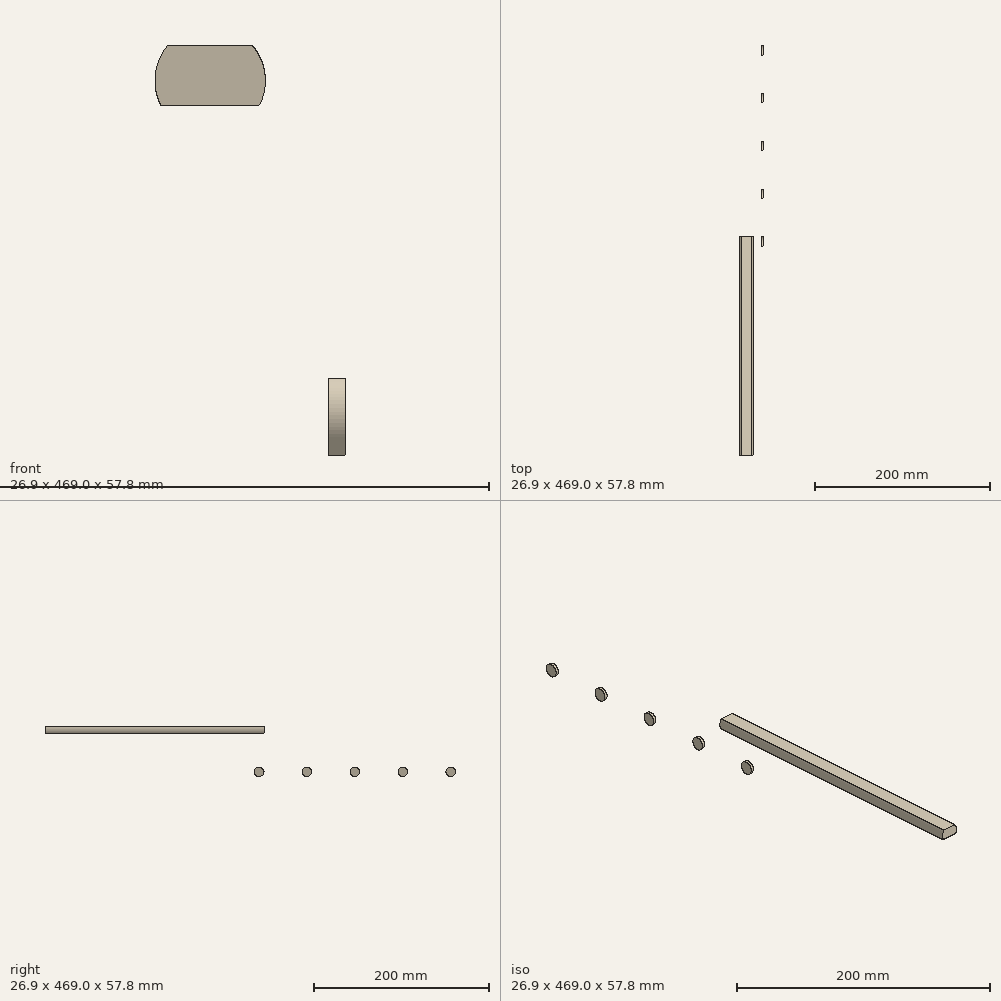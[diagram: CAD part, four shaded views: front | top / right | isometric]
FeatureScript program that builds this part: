
annotation { "Feature Type Name" : "Feature", "Feature Type Description" : "" }
export const myFeature = defineFeature(function(context is Context, id is Id, definition is map)
    precondition{}
    {
        {
            var Q0;
            Q0=qCreatedBy(makeId("Front.planeOp"),FACE);
            var sketch = newSketch(context, id + "F0", { "sketchPlane" : qUnion([Q0])});
            skLineSegment(sketch, "E0", {"start": v(-22.7, 21.08) * mm, "end": v(-10.77, 21.08) * mm});
            skLineSegment(sketch, "E1", {"start": v(-9.73, 12.68) * mm, "end": v(-23.73, 12.68) * mm});
            skLineSegment(sketch, "E2", {"start": v(-9.73, 19.48) * mm, "end": v(-9.73, 18.68) * mm});
            skLineSegment(sketch, "E3", {"start": v(-9.73, 18.68) * mm, "end": v(-9.73, 12.68) * mm});
            skLineSegment(sketch, "E4", {"start": v(-23.73, 19.48) * mm, "end": v(-23.73, 16.08) * mm});
            skPoint(sketch, "E5.endSnap0", {"position": v(-16.73, 21.08) * mm});
            skArc(sketch, "E6", {"start": v(-23.73, 12.68) * mm, "mid": v(-24.46, 17.04) * mm, "end": v(-22.7, 21.08) * mm});
            skArc(sketch, "E7.trimOffspring", {"start": v(-10.77, 21.08) * mm, "mid": v(-9.01, 17.04) * mm, "end": v(-9.73, 12.68) * mm});
            skPoint(sketch, "E8.orphan", {"position": v(-23.73, 21.08) * mm});
            skPoint(sketch, "E9.orphan", {"position": v(-9.73, 21.08) * mm});
            skSolve(sketch);
        }
        {
            var Q0;
            {var subQ2=sQuery(id+"F0.wireOp",EDGE,"E0");Q0=makeQuery(id+"F0.imprint","IMPRINT",FACE,{"disambiguationData":[TD([[makeQuery(id+"F0.imprint","IMPRINT",EDGE,{"derivedFrom":subQ2}),-1.0]])]});}
            var Q1;
            {var subQ0=sQuery(id+"F0.wireOp",EDGE,"E2");Q1=makeQuery(id+"F0.imprint","IMPRINT",FACE,{"disambiguationData":[TD([[makeQuery(id+"F0.imprint","IMPRINT",EDGE,{"derivedFrom":subQ0}),1.0]])]});}
            extrude(context, id + "F1", {"entities" : qUnion([Q0, Q1]), "depth" : 250 * mm, "offsetDistance" : 25 * mm});
        }
        {
            var Q0;
            Q0=qCreatedBy(makeId("Right.planeOp"),FACE);
            var sketch = newSketch(context, id + "F2", { "sketchPlane" : qUnion([Q0])});
            skCircle(sketch, "E10", {"center": v(-5.4, -31.27) * mm, "radius": 5.45 * mm});
            skCircle(sketch, "E11.1.0.0", {"center": v(49.34, -31.27) * mm, "radius": 5.45 * mm});
            skCircle(sketch, "E11.2.0.0", {"center": v(104.1, -31.27) * mm, "radius": 5.45 * mm});
            skCircle(sketch, "E11.3.0.0", {"center": v(158.84, -31.27) * mm, "radius": 5.45 * mm});
            skCircle(sketch, "E11.4.0.0", {"center": v(213.6, -31.27) * mm, "radius": 5.45 * mm});
            skLineSegment(sketch, "E11.direction1", {"start": v(-5.4, -31.27) * mm, "end": v(49.34, -31.27) * mm, "construction": true});
            skSolve(sketch);
        }
        {
            var Q0;
            Q0 = qSketchRegion(id + "F2", true);
            extrude(context, id + "F3", {"entities" : qUnion([Q0]), "depth" : 2.4 * mm, "offsetDistance" : 25 * mm});
        }
    });
